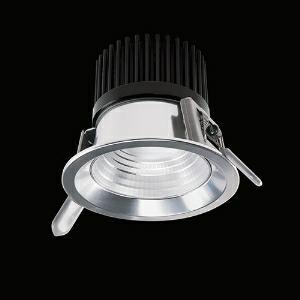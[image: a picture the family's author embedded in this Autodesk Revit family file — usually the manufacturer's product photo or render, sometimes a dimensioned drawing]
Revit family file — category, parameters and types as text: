
# Revit family: spectral_myral_myral_1500-830-f
name_source: partatom
category: Lighting Fixtures
revit_build: Autodesk Revit 2016 (Build: 20150220_1215(x64)
units: mm (PartAtom-declared; Revit-internal decimal feet)

## family parameters
Cut with Voids When Loaded = No
Host = Face
Light Source = No
Part Type = Normal
Room Calculation Point = No
Round Connector Dimension = Use Diameter
Shared = No

## types (1)
- SPECTRAL MYRAL (1 x )
    Apparent Load = 0 VA
    Approval mark = CE
    CIE Flux Codes = 81 99 100 100 100
    Control Gear = Electronic transformer
    Default Elevation = 1800 mm
    Description = SPG0320184
MYRAL recessed spot

Design:
    Height = 0 mm  [stored 0 ft]
    Lamp = 1 x
    Lamp count = 1
    Length = 120 mm
    Luminous efficacy = 0 lm/W
    Manufacturer = Ridi
    ModVariant = No
    Model = MYRAL 1500-830-F
    Mounting Place = Ceiling
    Mounting Type = Recessed
    Number of Poles = 1
    OnlyDefault = Yes
    Power Factor = 1
    Product Name = SPECTRAL MYRAL
    Product group = Downlight recessed
    ProductGroupID = 400
    Protection Class = Protection class
    Protection Degree = IP 20
    RlxData = <blob elided: 38885 chars, md5=43a4b3a5>
    Socket = socket
    Standby Power = 0 W
    System Light Flux = 0 lm
    System Power = 0 W
    Type Image = myral_04.jpg
    URL = http://reluxnet.relux.com
    VarID = ---
    Voltage = 0 V
    Weight = 0.00 kg
    Width = 0 mm  [stored 0 ft]

note: [stored X ft] marks values corroborated as IEEE doubles in the binary element streams (Revit-internal decimal feet)

## geometry (parser evidence)
native form markers: Sweep x12
no freeform markers — native parametric forms only
